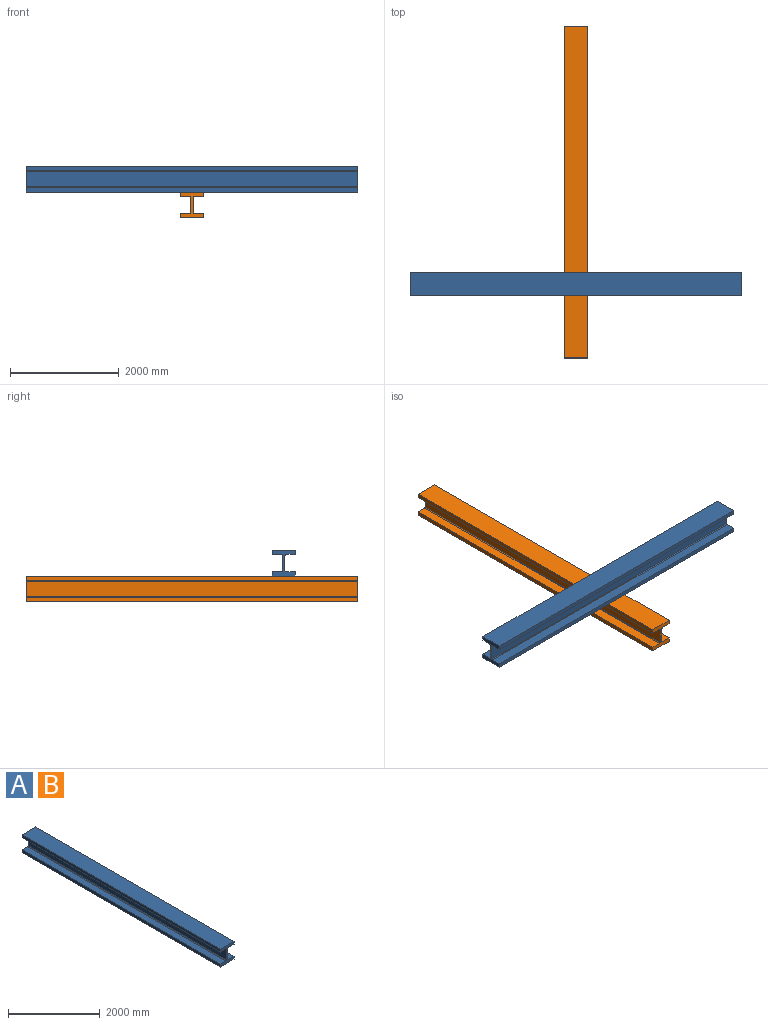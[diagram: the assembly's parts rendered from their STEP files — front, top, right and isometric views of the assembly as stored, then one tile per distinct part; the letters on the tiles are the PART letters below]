
ASSEMBLY  parts=2 mates=1
PART A: 18 faces, bbox 424.1x6096x474.2 mm
  f0: cylinder r=14.99mm len=6096mm, axis (0,1,0), area 143499.6mm2, adj f1,f15,f16,f17
  f1: plane 6096x290.07mm, normal (-1,0,0), area 1768254.5mm2, adj f0,f2,f16,f17
  f2: cylinder r=14.99mm len=6096mm, axis (0,1,0), area 143499.6mm2, adj f1,f3,f16,f17
  f3: plane 6096x173.23mm, normal (0,0,1), area 1055997.9mm2, adj f2,f4,f16,f17
  f4: plane 6096x77.09mm, normal (-1,0,0), area 469934.5mm2, adj f3,f5,f16,f17
  f5: plane 6096x424.05mm, normal (0,0,-1), area 2585027.1mm2, adj f4,f6,f16,f17
  f6: plane 6096x77.09mm, normal (1,0,0), area 469934.5mm2, adj f5,f7,f16,f17
  f7: plane 6096x173.23mm, normal (0,0,1), area 1055997.9mm2, adj f6,f8,f16,f17
  f8: cylinder r=14.99mm len=6096mm, axis (0,1,0), area 143499.6mm2, adj f7,f9,f16,f17
  f9: plane 6096x290.07mm, normal (1,0,0), area 1768254.5mm2, adj f8,f10,f16,f17
  f10: cylinder r=14.99mm len=6096mm, axis (0,1,0), area 143499.6mm2, adj f9,f11,f16,f17
  f11: plane 6096x173.23mm, normal (0,0,-1), area 1055997.9mm2, adj f10,f12,f16,f17
  f12: plane 6096x77.09mm, normal (1,0,0), area 469934.5mm2, adj f11,f13,f16,f17
  f13: plane 6096x424.05mm, normal (0,0,1), area 2585027.1mm2, adj f12,f14,f16,f17
  f14: plane 6096x77.09mm, normal (-1,0,0), area 469934.5mm2, adj f13,f15,f16,f17
  f15: plane 6096x173.23mm, normal (0,0,-1), area 1055997.9mm2, adj f0,f14,f16,f17
  f16: plane 474.22x424.05mm, normal (0,-1,0), area 80814.3mm2, adj f0,f1,f2,f3,f4,f5,f6,f7
  f17: plane 474.22x424.05mm, normal (0,1,0), area 80814.3mm2, adj f0,f1,f2,f3,f4,f5,f6,f7
PART B: same geometry as A
PLACE A rot(axis=(0,0,-1),90deg) t=(1630.95,-2892.52,-666.48)mm
PLACE B t=(-1629.08,1627.47,-1140.7)mm
MATE planar A.f5 <-> B.f13  axis (0,0,-1) through (-1417.05,-3104.55,-666.48)mm
